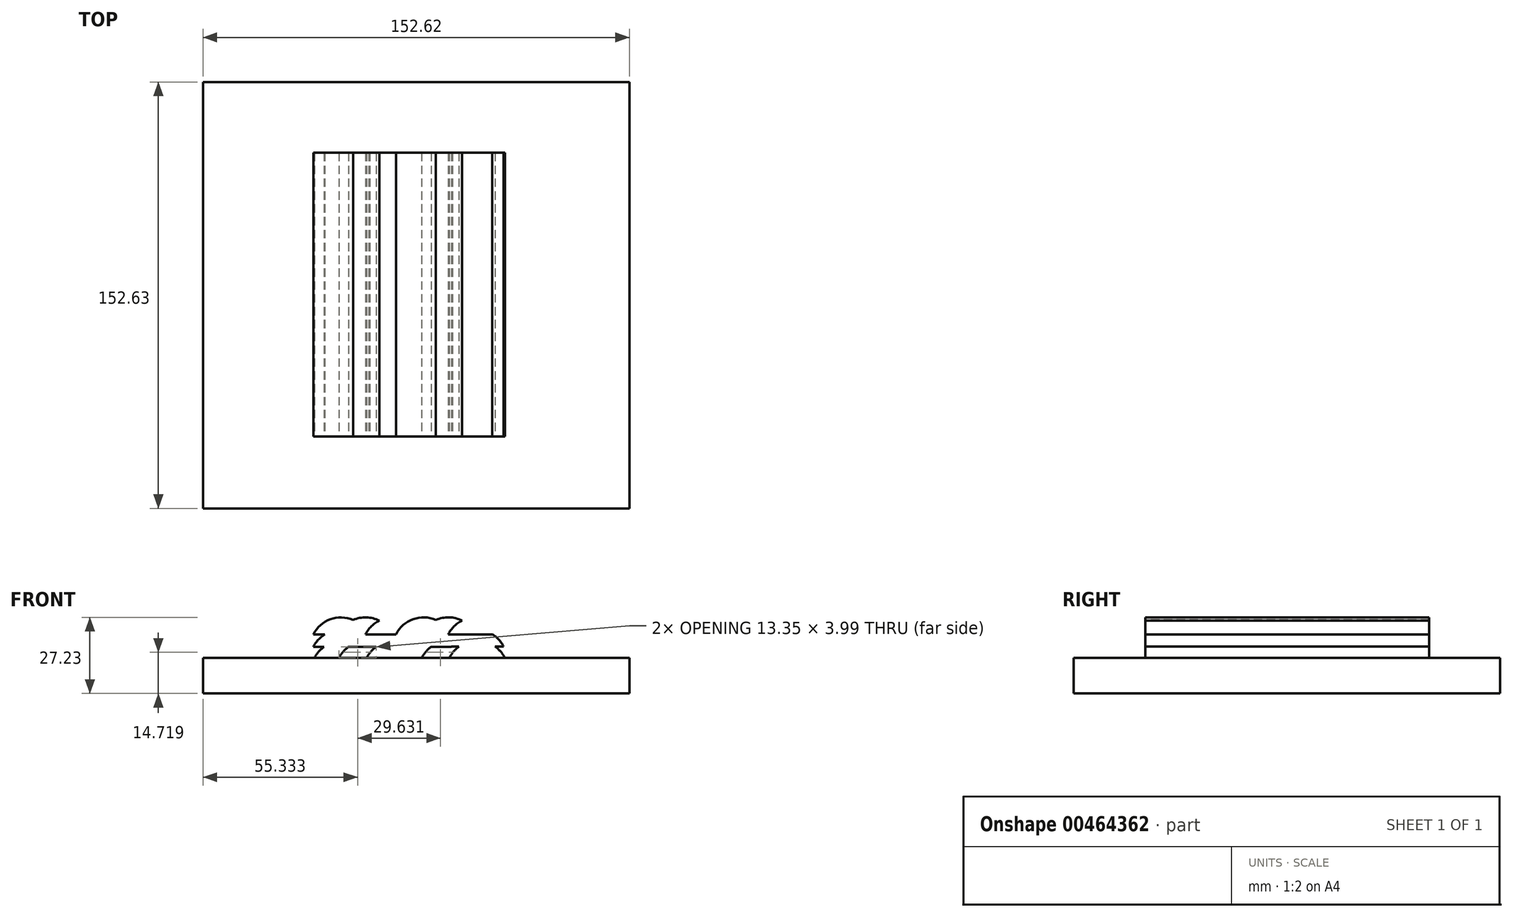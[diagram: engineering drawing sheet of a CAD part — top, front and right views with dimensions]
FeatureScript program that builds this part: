
annotation { "Feature Type Name" : "Feature", "Feature Type Description" : "" }
export const myFeature = defineFeature(function(context is Context, id is Id, definition is map)
    precondition{}
    {
        {
            var Q0;
            Q0=qCreatedBy(makeId("Top.planeOp"),FACE);
            var sketch = newSketch(context, id + "F0", { "sketchPlane" : qUnion([Q0])});
            skLineSegment(sketch, "E0.bottom", {"start": v(-75.96, 76.14) * mm, "end": v(76.66, 76.14) * mm});
            skLineSegment(sketch, "E0.top", {"start": v(-75.96, -76.49) * mm, "end": v(76.66, -76.49) * mm});
            skLineSegment(sketch, "E0.left", {"start": v(-75.96, 76.14) * mm, "end": v(-75.96, -76.49) * mm});
            skLineSegment(sketch, "E0.right", {"start": v(76.66, 76.14) * mm, "end": v(76.66, -76.49) * mm});
            skSolve(sketch);
        }
        {
            var Q0;
            Q0=makeQuery(id+"F0.imprint","IMPRINT",FACE,{"disambiguationData":[TD([[makeQuery(id+"F0.imprint","IMPRINT",EDGE,{"derivedFrom":sQuery(id+"F0.wireOp",EDGE,"E0.bottom")}),-1.0]])]});
            extrude(context, id + "F1", {"entities" : qUnion([Q0]), "depth" : 12.7 * mm});
        }
        {
            var Q0;
            Q0=qCreatedBy(makeId("Front.planeOp"),FACE);
            cPlane(context, id + "F2", {"entities" : qUnion([Q0]), "cplaneType" : CPlaneType.OFFSET, "offset" : 50.8 * mm, "width" : 152.4 * mm, "height" : 152.4 * mm});
        }
        {
            var Q0;
            Q0=qCreatedBy(id+"F2.planeOp",FACE);
            var sketch = newSketch(context, id + "F3", { "sketchPlane" : qUnion([Q0])});
            skLineSegment(sketch, "E1", {"start": v(-27.3, 12.72) * mm, "end": v(-7.48, 12.72) * mm});
            skLineSegment(sketch, "E2", {"start": v(-36.1, 12.7) * mm, "end": v(-16.27, 12.7) * mm});
            skArc(sketch, "E3", {"start": v(-16.27, 12.7) * mm, "mid": v(-16.28, 12.71) * mm, "end": v(-16.29, 12.72) * mm});
            skLineSegment(sketch, "E4", {"start": v(-17.4, 12.72) * mm, "end": v(2.43, 12.72) * mm});
            skLineSegment(sketch, "E5", {"start": v(2.33, 12.75) * mm, "end": v(22.15, 12.75) * mm});
            skLineSegment(sketch, "E6", {"start": v(-6.46, 12.72) * mm, "end": v(13.36, 12.72) * mm});
            skArc(sketch, "E7", {"start": v(13.36, 12.72) * mm, "mid": v(13.35, 12.74) * mm, "end": v(13.34, 12.75) * mm});
            skLineSegment(sketch, "E8", {"start": v(12.24, 12.75) * mm, "end": v(32.06, 12.75) * mm});
            skArc(sketch, "E9", {"start": v(32.06, 12.75) * mm, "mid": v(30.58, 14.95) * mm, "end": v(28.63, 16.74) * mm});
            skLineSegment(sketch, "E10", {"start": v(-27.7, 16.71) * mm, "end": v(-7.87, 16.71) * mm});
            skLineSegment(sketch, "E11", {"start": v(-36.49, 16.69) * mm, "end": v(-16.67, 16.69) * mm});
            skArc(sketch, "E12", {"start": v(-16.67, 16.69) * mm, "mid": v(-16.67, 16.7) * mm, "end": v(-16.68, 16.71) * mm});
            skLineSegment(sketch, "E13", {"start": v(-17.78, 16.71) * mm, "end": v(2.04, 16.71) * mm});
            skArc(sketch, "E14", {"start": v(2.04, 16.71) * mm, "mid": v(2.01, 16.77) * mm, "end": v(1.98, 16.82) * mm});
            skLineSegment(sketch, "E15", {"start": v(1.94, 16.74) * mm, "end": v(21.76, 16.74) * mm});
            skLineSegment(sketch, "E16", {"start": v(-6.86, 16.71) * mm, "end": v(12.96, 16.71) * mm});
            skArc(sketch, "E17", {"start": v(12.96, 16.71) * mm, "mid": v(12.96, 16.73) * mm, "end": v(12.95, 16.74) * mm});
            skLineSegment(sketch, "E18", {"start": v(11.85, 16.74) * mm, "end": v(31.67, 16.74) * mm});
            skArc(sketch, "E19", {"start": v(31.67, 16.74) * mm, "mid": v(29.93, 19.23) * mm, "end": v(27.58, 21.16) * mm});
            skLineSegment(sketch, "E20", {"start": v(-27.72, 21.14) * mm, "end": v(-7.9, 21.14) * mm});
            skArc(sketch, "E21", {"start": v(-12.86, 26.04) * mm, "mid": v(-21.3, 26.65) * mm, "end": v(-27.72, 21.14) * mm});
            skLineSegment(sketch, "E22", {"start": v(-36.52, 21.11) * mm, "end": v(-16.7, 21.11) * mm});
            skArc(sketch, "E23", {"start": v(-16.7, 21.11) * mm, "mid": v(-16.7, 21.13) * mm, "end": v(-16.71, 21.14) * mm});
            skLineSegment(sketch, "E24", {"start": v(-17.81, 21.14) * mm, "end": v(2, 21.14) * mm});
            skArc(sketch, "E25", {"start": v(2, 21.14) * mm, "mid": v(1.98, 21.2) * mm, "end": v(1.95, 21.25) * mm});
            skLineSegment(sketch, "E26", {"start": v(1.9, 21.16) * mm, "end": v(21.73, 21.16) * mm});
            skArc(sketch, "E27", {"start": v(16.77, 26.07) * mm, "mid": v(8.33, 26.67) * mm, "end": v(1.9, 21.16) * mm});
            skLineSegment(sketch, "E28", {"start": v(-6.89, 21.14) * mm, "end": v(12.93, 21.14) * mm});
            skArc(sketch, "E29", {"start": v(12.93, 21.14) * mm, "mid": v(12.93, 21.15) * mm, "end": v(12.92, 21.16) * mm});
            skLineSegment(sketch, "E30", {"start": v(11.82, 21.16) * mm, "end": v(31.64, 21.16) * mm});
            skArc(sketch, "E31", {"start": v(31.64, 21.16) * mm, "mid": v(21.73, 27.23) * mm, "end": v(11.82, 21.16) * mm});
            skArc(sketch, "E32.trimOffspring", {"start": v(-19.71, 16.69) * mm, "mid": v(-19.73, 16.7) * mm, "end": v(-19.75, 16.71) * mm});
            skArc(sketch, "E33.trimOffspring", {"start": v(9.92, 16.71) * mm, "mid": v(9.9, 16.73) * mm, "end": v(9.89, 16.74) * mm});
            skArc(sketch, "E34.trimOffspring", {"start": v(-32.66, 16.69) * mm, "mid": v(-34.62, 14.9) * mm, "end": v(-36.1, 12.7) * mm});
            skArc(sketch, "E35.trimOffspring", {"start": v(-23.86, 16.71) * mm, "mid": v(-25.82, 14.93) * mm, "end": v(-27.3, 12.72) * mm});
            skArc(sketch, "E36.trimOffspring", {"start": v(-20.75, 21.11) * mm, "mid": v(-20.77, 21.13) * mm, "end": v(-20.8, 21.14) * mm});
            skArc(sketch, "E37.trimOffspring", {"start": v(8.88, 21.14) * mm, "mid": v(8.86, 21.15) * mm, "end": v(8.84, 21.16) * mm});
            skArc(sketch, "E38.trimOffspring", {"start": v(-13.95, 16.71) * mm, "mid": v(-15.91, 14.93) * mm, "end": v(-17.4, 12.72) * mm});
            skArc(sketch, "E39.trimOffspring", {"start": v(-3.03, 16.71) * mm, "mid": v(-4.99, 14.93) * mm, "end": v(-6.46, 12.72) * mm});
            skArc(sketch, "E40.trimOffspring", {"start": v(5.77, 16.74) * mm, "mid": v(3.8, 14.95) * mm, "end": v(2.33, 12.75) * mm});
            skArc(sketch, "E41.trimOffspring", {"start": v(15.68, 16.74) * mm, "mid": v(13.72, 14.95) * mm, "end": v(12.24, 12.75) * mm});
            skArc(sketch, "E42.trimOffspring", {"start": v(-32.4, 21.11) * mm, "mid": v(-34.75, 19.18) * mm, "end": v(-36.49, 16.69) * mm});
            skArc(sketch, "E43.trimOffspring", {"start": v(-22.24, 26.29) * mm, "mid": v(-30.4, 26.52) * mm, "end": v(-36.52, 21.11) * mm});
            skArc(sketch, "E44.trimOffspring", {"start": v(-23.6, 21.14) * mm, "mid": v(-25.95, 19.2) * mm, "end": v(-27.7, 16.71) * mm});
            skArc(sketch, "E45.trimOffspring", {"start": v(-13.7, 21.14) * mm, "mid": v(-16.04, 19.2) * mm, "end": v(-17.78, 16.71) * mm});
            skArc(sketch, "E46.trimOffspring", {"start": v(-2.77, 21.14) * mm, "mid": v(-5.12, 19.2) * mm, "end": v(-6.86, 16.71) * mm});
            skArc(sketch, "E47.trimOffspring", {"start": v(-2.44, 25.77) * mm, "mid": v(-11.11, 26.73) * mm, "end": v(-17.81, 21.14) * mm});
            skArc(sketch, "E48.trimOffspring", {"start": v(6.03, 21.16) * mm, "mid": v(3.68, 19.23) * mm, "end": v(1.94, 16.74) * mm});
            skArc(sketch, "E49.trimOffspring", {"start": v(7.4, 26.31) * mm, "mid": v(-0.77, 26.54) * mm, "end": v(-6.89, 21.14) * mm});
            skArc(sketch, "E50.trimOffspring", {"start": v(15.94, 21.16) * mm, "mid": v(13.59, 19.23) * mm, "end": v(11.85, 16.74) * mm});
            skSolve(sketch);
        }
        {
            var Q0;
            {var subQ9=sQuery(id+"F3.wireOp",EDGE,"E23");Q0=makeQuery(id+"F3.imprint","IMPRINT",FACE,{"disambiguationData":[TD([[makeQuery(id+"F3.imprint","IMPRINT",EDGE,{"derivedFrom":subQ9}),-1.0]])]});}
            var Q1;
            {var subQ0=sQuery(id+"F3.wireOp",EDGE,"E30");var subQ2=makeQuery(id+"F3.imprint","IMPRINT",VERTEX,{"derivedFrom":subQ0});Q1=makeQuery(id+"F3.imprint","IMPRINT",FACE,{"disambiguationData":[TD([[makeQuery(id+"F3.imprint","IMPRINT",EDGE,{"disambiguationData":[TD([[subQ2,1.0]])],"derivedFrom":subQ0}),1.0]])]});}
            var Q2;
            {var subQ0=sQuery(id+"F3.wireOp",EDGE,"E42.trimOffspring");Q2=makeQuery(id+"F3.imprint","IMPRINT",FACE,{"disambiguationData":[TD([[makeQuery(id+"F3.imprint","IMPRINT",EDGE,{"derivedFrom":subQ0}),1.0]])]});}
            var Q3;
            {var subQ1=sQuery(id+"F3.wireOp",EDGE,"E24");var subQ3=makeQuery(id+"F3.imprint","IMPRINT",VERTEX,{"derivedFrom":subQ1});Q3=makeQuery(id+"F3.imprint","IMPRINT",FACE,{"disambiguationData":[TD([[makeQuery(id+"F3.imprint","IMPRINT",EDGE,{"disambiguationData":[TD([[subQ3,1.0]])],"derivedFrom":subQ1}),1.0]])]});}
            var Q4;
            {var subQ6=sQuery(id+"F3.wireOp",EDGE,"E19");Q4=makeQuery(id+"F3.imprint","IMPRINT",FACE,{"disambiguationData":[TD([[makeQuery(id+"F3.imprint","IMPRINT",EDGE,{"derivedFrom":subQ6}),1.0]])]});}
            var Q5;
            {var subQ5=sQuery(id+"F3.wireOp",EDGE,"E25");var subQ7=sQuery(id+"F3.wireOp",EDGE,"E27");var subQ8=makeQuery(id+"F3.imprint","INTERSECT",VERTEX,{"derivedFrom":[subQ5,subQ7]});Q5=makeQuery(id+"F3.imprint","IMPRINT",FACE,{"disambiguationData":[TD([[makeQuery(id+"F3.imprint","IMPRINT",EDGE,{"disambiguationData":[TD([[subQ8,1.0]])],"derivedFrom":subQ5}),-1.0]])]});}
            var Q6;
            {var subQ1=sQuery(id+"F3.wireOp",EDGE,"E21");var subQ4=sQuery(id+"F3.wireOp",EDGE,"E20");var subQ8=makeQuery(id+"F3.imprint","INTERSECT",VERTEX,{"derivedFrom":[subQ4,subQ1]});Q6=makeQuery(id+"F3.imprint","IMPRINT",FACE,{"disambiguationData":[TD([[makeQuery(id+"F3.imprint","IMPRINT",EDGE,{"disambiguationData":[TD([[subQ8,-1.0]])],"derivedFrom":subQ4}),1.0]])]});}
            var Q7;
            {var subQ1=sQuery(id+"F3.wireOp",EDGE,"E25");var subQ9=sQuery(id+"F3.wireOp",EDGE,"E28");var subQ10=makeQuery(id+"F3.imprint","INTERSECT",VERTEX,{"derivedFrom":[subQ1,subQ9]});Q7=makeQuery(id+"F3.imprint","IMPRINT",FACE,{"disambiguationData":[TD([[makeQuery(id+"F3.imprint","IMPRINT",EDGE,{"disambiguationData":[TD([[subQ10,-1.0]])],"derivedFrom":subQ1}),1.0]])]});}
            var Q8;
            {var subQ9=sQuery(id+"F3.wireOp",EDGE,"E45.trimOffspring");Q8=makeQuery(id+"F3.imprint","IMPRINT",FACE,{"disambiguationData":[TD([[makeQuery(id+"F3.imprint","IMPRINT",EDGE,{"derivedFrom":subQ9}),1.0]])]});}
            var Q9;
            {var subQ5=sQuery(id+"F3.wireOp",EDGE,"E29");Q9=makeQuery(id+"F3.imprint","IMPRINT",FACE,{"disambiguationData":[TD([[makeQuery(id+"F3.imprint","IMPRINT",EDGE,{"derivedFrom":subQ5}),-1.0]])]});}
            var Q10;
            {var subQ0=sQuery(id+"F3.wireOp",EDGE,"E46.trimOffspring");Q10=makeQuery(id+"F3.imprint","IMPRINT",FACE,{"disambiguationData":[TD([[makeQuery(id+"F3.imprint","IMPRINT",EDGE,{"derivedFrom":subQ0}),1.0]])]});}
            var Q11;
            {var subQ4=sQuery(id+"F3.wireOp",EDGE,"E43.trimOffspring");Q11=makeQuery(id+"F3.imprint","IMPRINT",FACE,{"disambiguationData":[TD([[makeQuery(id+"F3.imprint","IMPRINT",EDGE,{"derivedFrom":subQ4}),1.0]])]});}
            var Q12;
            {var subQ0=sQuery(id+"F3.wireOp",EDGE,"E36.trimOffspring");Q12=makeQuery(id+"F3.imprint","IMPRINT",FACE,{"disambiguationData":[TD([[makeQuery(id+"F3.imprint","IMPRINT",EDGE,{"derivedFrom":subQ0}),1.0]])]});}
            var Q13;
            {var subQ3=sQuery(id+"F3.wireOp",EDGE,"E23");Q13=makeQuery(id+"F3.imprint","IMPRINT",FACE,{"disambiguationData":[TD([[makeQuery(id+"F3.imprint","IMPRINT",EDGE,{"derivedFrom":subQ3}),1.0]])]});}
            var Q14;
            {var subQ0=sQuery(id+"F3.wireOp",EDGE,"E32.trimOffspring");Q14=makeQuery(id+"F3.imprint","IMPRINT",FACE,{"disambiguationData":[TD([[makeQuery(id+"F3.imprint","IMPRINT",EDGE,{"derivedFrom":subQ0}),1.0]])]});}
            var Q15;
            {var subQ0=sQuery(id+"F3.wireOp",EDGE,"E37.trimOffspring");Q15=makeQuery(id+"F3.imprint","IMPRINT",FACE,{"disambiguationData":[TD([[makeQuery(id+"F3.imprint","IMPRINT",EDGE,{"derivedFrom":subQ0}),1.0]])]});}
            var Q16;
            {var subQ3=sQuery(id+"F3.wireOp",EDGE,"E12");Q16=makeQuery(id+"F3.imprint","IMPRINT",FACE,{"disambiguationData":[TD([[makeQuery(id+"F3.imprint","IMPRINT",EDGE,{"derivedFrom":subQ3}),1.0]])]});}
            var Q17;
            {var subQ0=sQuery(id+"F3.wireOp",EDGE,"E28");var subQ1=sQuery(id+"F3.wireOp",EDGE,"E25");var subQ2=makeQuery(id+"F3.imprint","INTERSECT",VERTEX,{"derivedFrom":[subQ1,subQ0]});Q17=makeQuery(id+"F3.imprint","IMPRINT",FACE,{"disambiguationData":[TD([[makeQuery(id+"F3.imprint","IMPRINT",EDGE,{"disambiguationData":[TD([[subQ2,-1.0]])],"derivedFrom":subQ1}),-1.0]])]});}
            var Q18;
            {var subQ3=sQuery(id+"F3.wireOp",EDGE,"E17");Q18=makeQuery(id+"F3.imprint","IMPRINT",FACE,{"disambiguationData":[TD([[makeQuery(id+"F3.imprint","IMPRINT",EDGE,{"derivedFrom":subQ3}),1.0]])]});}
            var Q19;
            {var subQ0=sQuery(id+"F3.wireOp",EDGE,"E16");var subQ1=sQuery(id+"F3.wireOp",EDGE,"E14");var subQ2=makeQuery(id+"F3.imprint","INTERSECT",VERTEX,{"derivedFrom":[subQ1,subQ0]});Q19=makeQuery(id+"F3.imprint","IMPRINT",FACE,{"disambiguationData":[TD([[makeQuery(id+"F3.imprint","IMPRINT",EDGE,{"disambiguationData":[TD([[subQ2,-1.0]])],"derivedFrom":subQ1}),-1.0]])]});}
            var Q20;
            {var subQ0=sQuery(id+"F3.wireOp",EDGE,"E33.trimOffspring");Q20=makeQuery(id+"F3.imprint","IMPRINT",FACE,{"disambiguationData":[TD([[makeQuery(id+"F3.imprint","IMPRINT",EDGE,{"derivedFrom":subQ0}),1.0]])]});}
            var Q21;
            {var subQ0=sQuery(id+"F3.wireOp",EDGE,"E29");Q21=makeQuery(id+"F3.imprint","IMPRINT",FACE,{"disambiguationData":[TD([[makeQuery(id+"F3.imprint","IMPRINT",EDGE,{"derivedFrom":subQ0}),1.0]])]});}
            var Q22;
            {var subQ0=sQuery(id+"F3.wireOp",EDGE,"E48.trimOffspring");var subQ1=sQuery(id+"F3.wireOp",EDGE,"E14");var subQ2=makeQuery(id+"F3.imprint","INTERSECT",VERTEX,{"derivedFrom":[subQ1,subQ0]});Q22=makeQuery(id+"F3.imprint","IMPRINT",FACE,{"disambiguationData":[TD([[makeQuery(id+"F3.imprint","IMPRINT",EDGE,{"disambiguationData":[TD([[subQ2,1.0]])],"derivedFrom":subQ1}),1.0]])]});}
            var Q23;
            {var subQ0=sQuery(id+"F3.wireOp",EDGE,"E27");var subQ1=sQuery(id+"F3.wireOp",EDGE,"E25");var subQ2=makeQuery(id+"F3.imprint","INTERSECT",VERTEX,{"derivedFrom":[subQ1,subQ0]});Q23=makeQuery(id+"F3.imprint","IMPRINT",FACE,{"disambiguationData":[TD([[makeQuery(id+"F3.imprint","IMPRINT",EDGE,{"disambiguationData":[TD([[subQ2,1.0]])],"derivedFrom":subQ1}),1.0]])]});}
            var Q24;
            {var subQ1=sQuery(id+"F3.wireOp",EDGE,"E1");Q24=makeQuery(id+"F3.imprint","IMPRINT",FACE,{"disambiguationData":[TD([[makeQuery(id+"F3.imprint","IMPRINT",EDGE,{"derivedFrom":subQ1}),-1.0]])]});}
            var Q25;
            {var subQ1=sQuery(id+"F3.wireOp",EDGE,"E1");Q25=makeQuery(id+"F3.imprint","IMPRINT",FACE,{"disambiguationData":[TD([[makeQuery(id+"F3.imprint","IMPRINT",EDGE,{"derivedFrom":subQ1}),1.0]])]});}
            var Q26;
            {var subQ7=sQuery(id+"F3.wireOp",EDGE,"E38.trimOffspring");Q26=makeQuery(id+"F3.imprint","IMPRINT",FACE,{"disambiguationData":[TD([[makeQuery(id+"F3.imprint","IMPRINT",EDGE,{"derivedFrom":subQ7}),1.0]])]});}
            var Q27;
            {var subQ2=sQuery(id+"F3.wireOp",EDGE,"E39.trimOffspring");Q27=makeQuery(id+"F3.imprint","IMPRINT",FACE,{"disambiguationData":[TD([[makeQuery(id+"F3.imprint","IMPRINT",EDGE,{"derivedFrom":subQ2}),1.0]])]});}
            var Q28;
            {var subQ3=sQuery(id+"F3.wireOp",EDGE,"E9");Q28=makeQuery(id+"F3.imprint","IMPRINT",FACE,{"disambiguationData":[TD([[makeQuery(id+"F3.imprint","IMPRINT",EDGE,{"derivedFrom":subQ3}),1.0]])]});}
            var Q29;
            {var subQ6=sQuery(id+"F3.wireOp",EDGE,"E5");Q29=makeQuery(id+"F3.imprint","IMPRINT",FACE,{"disambiguationData":[TD([[makeQuery(id+"F3.imprint","IMPRINT",EDGE,{"derivedFrom":subQ6}),1.0]])]});}
            extrude(context, id + "F4", {"entities" : qUnion([Q0, Q1, Q2, Q3, Q4, Q5, Q6, Q7, Q8, Q9, Q10, Q11, Q12, Q13, Q14, Q15, Q16, Q17, Q18, Q19, Q20, Q21, Q22, Q23, Q24, Q25, Q26, Q27, Q28, Q29]), "oppositeDirection" : true, "depth" : 101.6 * mm});
        }
    });
